# Revit family: QF_Vivreau_PURITY C500 Quell ST Advanced
name_source: partatom
category: Specialty Equipment
units: mm (PartAtom-declared; Revit-internal decimal feet)

## family parameters
Always vertical = Yes
Cut with Voids When Loaded = No
OmniClass Number = 23.40.40.14.24
OmniClass Title = Food Dispensing Equipment
Part Type = Normal
Room Calculation Point = No
Round Connector Dimension = Use Diameter
Shared = No
Work Plane-Based = No

## types (1)
- QF_Vivreau_PURITY C500 Quell ST Advanced
    Assembly Code = E1090320
    CSI MasterFormat = 11 46 00
    Cold Water Connection Height = 1' - 9"
    Cold Water Flow = 0.440 GPM
    Cold Water Maximum Pressure = 124.00 psi
    Cold Water Minimum Pressure = 29.00 psi
    Cold Water RI Height = 0' - 0"
    Cold Water Size = 1"
    Cold Water Temperature Recommended = 40 °F
    Default Elevation = 0' - 0"
    Depth = 0' - 5 7/8"
    Description = Water Filter
    Foodservice Equipment Identifier = Yes
    Height = 1' - 9 25/32"
    Identify Quantity as Lot = Yes
    Manufacturer = Vivreau
    Masterspec = Division 11
    Model = PURITY C500 Quell ST Advanced
    Plumbing Connection Type = NPT
    Specification by Manufacturer = (1054237) Vivreau Purity C500 Quell ST ADVANCED Filter Exchange cartridge, up to 1,796 gallons capacity, catalytic carbon, ion exchange for scale, chloramine protection, taste, odor NSF (NET)
    URL = https://vivreauwater.com
    URL Cutsheet = https://vivreauwater.com
    Weight in Pounds = 10.14
    Width = 0' - 5 7/8"

## geometry (parser evidence)
native form markers: Sweep x9
no freeform markers — native parametric forms only
